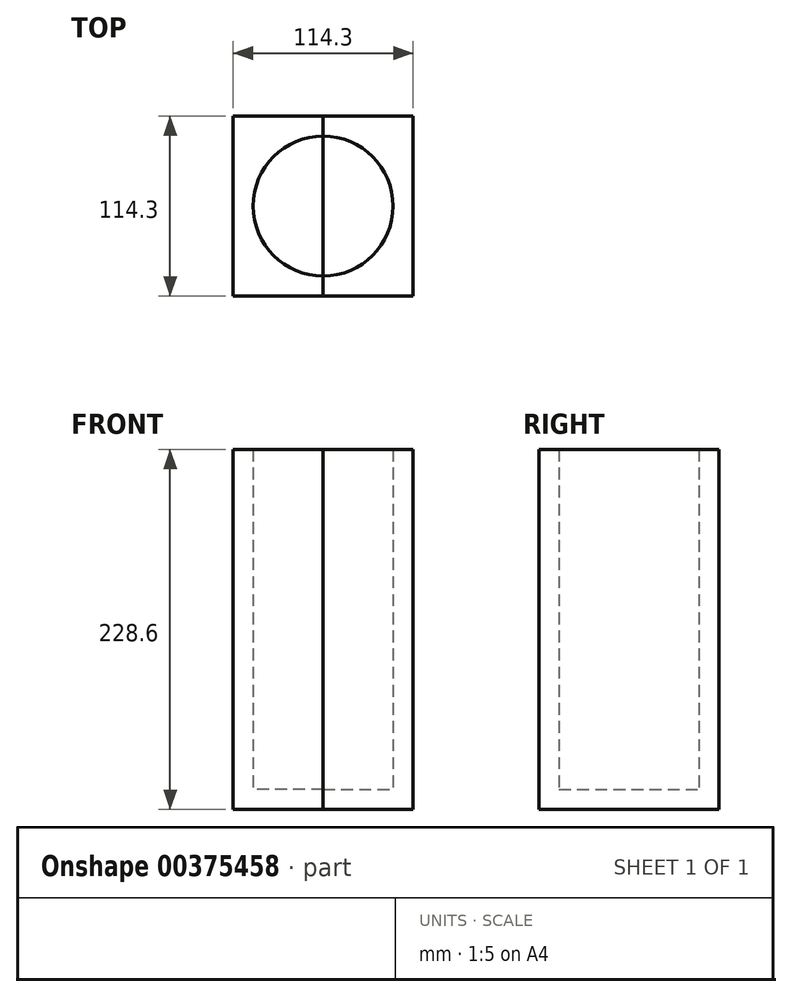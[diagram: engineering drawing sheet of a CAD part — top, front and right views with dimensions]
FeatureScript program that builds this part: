
annotation { "Feature Type Name" : "Feature", "Feature Type Description" : "" }
export const myFeature = defineFeature(function(context is Context, id is Id, definition is map)
    precondition{}
    {
        {
            var Q0;
            Q0=qCreatedBy(makeId("Top.planeOp"),FACE);
            var sketch = newSketch(context, id + "F0", { "sketchPlane" : qUnion([Q0])});
            skLineSegment(sketch, "E0.bottom", {"start": v(0, -57.15) * mm, "end": v(-63.5, -57.15) * mm});
            skLineSegment(sketch, "E0.top", {"start": v(0, 57.15) * mm, "end": v(-63.5, 57.15) * mm});
            skLineSegment(sketch, "E0.left", {"start": v(0, -57.15) * mm, "end": v(0, 57.15) * mm});
            skLineSegment(sketch, "E0.right", {"start": v(-63.5, -57.15) * mm, "end": v(-63.5, 57.15) * mm});
            skPoint(sketch, "E0.middle", {"position": v(-31.75, 0) * mm});
            skPoint(sketch, "E1.MirrorP", {"position": v(31.75, 0) * mm});
            skLineSegment(sketch, "E2.MirrorCS", {"start": v(0, -57.15) * mm, "end": v(63.5, -57.15) * mm});
            skLineSegment(sketch, "E3.MirrorCS", {"start": v(0, 57.15) * mm, "end": v(63.5, 57.15) * mm});
            skLineSegment(sketch, "E4.MirrorCS", {"start": v(63.5, -57.15) * mm, "end": v(63.5, 57.15) * mm});
            skSolve(sketch);
        }
        {
            var Q0;
            Q0=makeQuery(id+"F0.imprint","IMPRINT",FACE,{"disambiguationData":[TD([[makeQuery(id+"F0.imprint","IMPRINT",EDGE,{"derivedFrom":sQuery(id+"F0.wireOp",EDGE,"E0.bottom")}),-1.0]])]});
            extrude(context, id + "F1", {"entities" : qUnion([Q0]), "depth" : 228.6 * mm});
        }
        {
            var Q0;
            Q0=makeQuery(id+"F0.imprint","IMPRINT",FACE,{"disambiguationData":[TD([[makeQuery(id+"F0.imprint","IMPRINT",EDGE,{"derivedFrom":sQuery(id+"F0.wireOp",EDGE,"E2.MirrorCS")}),1.0]])]});
            extrude(context, id + "F2", {"entities" : qUnion([Q0]), "depth" : 228.6 * mm});
        }
        {
            var Q0;
            Q0=qCreatedBy(makeId("Top.planeOp"),FACE);
            cPlane(context, id + "F3", {"entities" : qUnion([Q0]), "cplaneType" : CPlaneType.OFFSET, "offset" : 12.7 * mm, "width" : 152.4 * mm, "height" : 152.4 * mm});
        }
        {
            var Q0;
            Q0=qCreatedBy(id+"F3.planeOp",FACE);
            var sketch = newSketch(context, id + "F4", { "sketchPlane" : qUnion([Q0])});
            skCircle(sketch, "E5", {"center": v(0, 0) * mm, "radius": 41.28 * mm});
            skCircle(sketch, "E6", {"center": v(0, 0) * mm, "radius": 44.45 * mm});
            skSolve(sketch);
        }
        {
            var Q0;
            Q0=makeQuery(id+"F4.imprint","IMPRINT",FACE,{"disambiguationData":[TD([[makeQuery(id+"F4.imprint","IMPRINT",EDGE,{"derivedFrom":sQuery(id+"F4.wireOp",EDGE,"E5")}),1.0]])]});
            extrude(context, id + "F5", {"entities" : qUnion([Q0]), "depth" : 203.2 * mm});
        }
        {
            var Q0;
            Q0=makeQuery(id+"F4.imprint","IMPRINT",FACE,{"disambiguationData":[TD([[makeQuery(id+"F4.imprint","IMPRINT",EDGE,{"derivedFrom":sQuery(id+"F4.wireOp",EDGE,"E5")}),-1.0]])]});
            var Q1;
            Q1=makeQuery(id+"F4.imprint","IMPRINT",FACE,{"disambiguationData":[TD([[makeQuery(id+"F4.imprint","IMPRINT",EDGE,{"derivedFrom":sQuery(id+"F4.wireOp",EDGE,"E5")}),1.0]])]});
            var Q2;
            Q2=makeQuery(id+"F1.opExtrude","CAP_FACE",FACE,{"disambiguationData":[OSD([sQuery(id+"F0.wireOp",EDGE,"E0.bottom"),sQuery(id+"F0.wireOp",EDGE,"E0.top"),sQuery(id+"F0.wireOp",EDGE,"E0.right"),sQuery(id+"F0.wireOp",EDGE,"E0.left")])],"isStart":false});
            extrude(context, id + "F6", {"entities" : qUnion([Q0, Q1]), "operationType" : NewBodyOperationType.REMOVE, "endBound" : BoundingType.UP_TO_SURFACE, "endBoundEntityFace" : qUnion([Q2]), "depth" : 25.4 * mm});
        }
        {
            var Q0;
            Q0=qCreatedBy(makeId("Top.planeOp"),FACE);
            var sketch = newSketch(context, id + "F7", { "sketchPlane" : qUnion([Q0])});
            skLineSegment(sketch, "E7.bottom", {"start": v(57.15, -57.15) * mm, "end": v(-57.15, -57.15) * mm});
            skLineSegment(sketch, "E7.top", {"start": v(57.15, 57.15) * mm, "end": v(-57.15, 57.15) * mm});
            skLineSegment(sketch, "E7.left", {"start": v(57.15, -57.15) * mm, "end": v(57.15, 57.15) * mm});
            skLineSegment(sketch, "E7.right", {"start": v(-57.15, -57.15) * mm, "end": v(-57.15, 57.15) * mm});
            skPoint(sketch, "E7.middle", {"position": v(0, 0) * mm});
            skLineSegment(sketch, "E8.bottom", {"start": v(63.5, -57.15) * mm, "end": v(-63.5, -57.15) * mm});
            skLineSegment(sketch, "E8.top", {"start": v(63.5, 57.15) * mm, "end": v(-63.5, 57.15) * mm});
            skLineSegment(sketch, "E8.left", {"start": v(63.5, -57.15) * mm, "end": v(63.5, 57.15) * mm});
            skLineSegment(sketch, "E8.right", {"start": v(-63.5, -57.15) * mm, "end": v(-63.5, 57.15) * mm});
            skSolve(sketch);
        }
        {
            var Q0;
            {var subQ0=sQuery(id+"F7.wireOp",EDGE,"E7.right");Q0=makeQuery(id+"F7.imprint","IMPRINT",FACE,{"disambiguationData":[TD([[makeQuery(id+"F7.imprint","IMPRINT",EDGE,{"derivedFrom":subQ0}),1.0]])]});}
            var Q1;
            {var subQ0=sQuery(id+"F7.wireOp",EDGE,"E7.left");Q1=makeQuery(id+"F7.imprint","IMPRINT",FACE,{"disambiguationData":[TD([[makeQuery(id+"F7.imprint","IMPRINT",EDGE,{"derivedFrom":subQ0}),-1.0]])]});}
            extrude(context, id + "F8", {"entities" : qUnion([Q0, Q1]), "operationType" : NewBodyOperationType.REMOVE, "endBound" : BoundingType.THROUGH_ALL, "depth" : 25.4 * mm});
        }
    });
